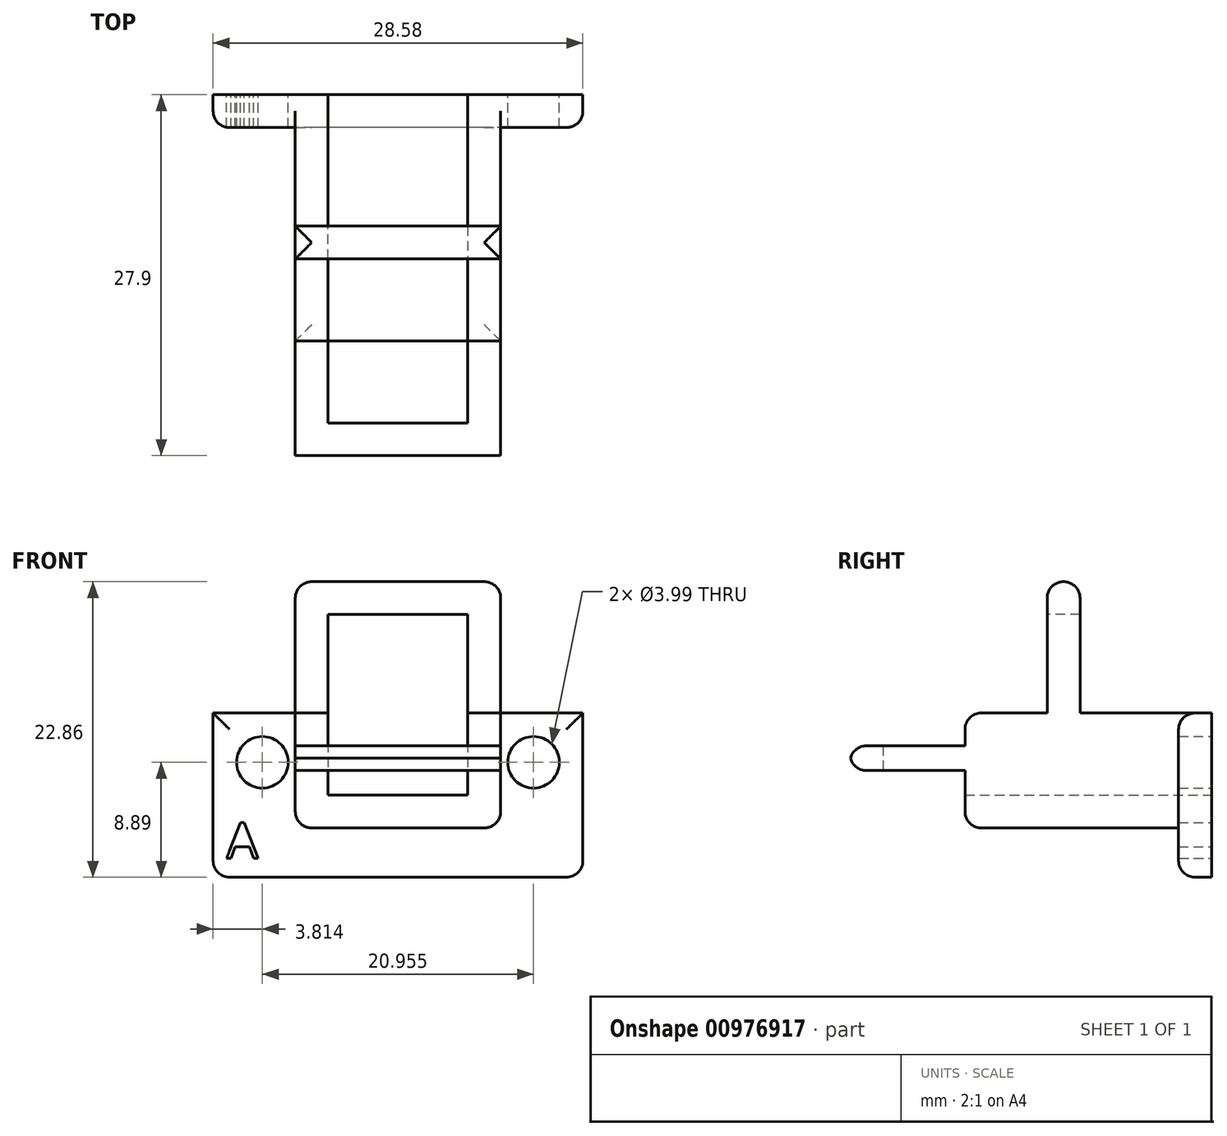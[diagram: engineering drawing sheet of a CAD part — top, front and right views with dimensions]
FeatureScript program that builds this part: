
annotation { "Feature Type Name" : "Feature", "Feature Type Description" : "" }
export const myFeature = defineFeature(function(context is Context, id is Id, definition is map)
    precondition{}
    {
        {
            var Q0;
            Q0=qCreatedBy(makeId("Front.planeOp"),FACE);
            var sketch = newSketch(context, id + "F0", { "sketchPlane" : qUnion([Q0])});
            skLineSegment(sketch, "E0", {"start": v(-23.2, 0) * mm, "end": v(-23.2, -6.35) * mm});
            skLineSegment(sketch, "E1", {"start": v(-12.41, 0) * mm, "end": v(-12.41, -6.35) * mm});
            skLineSegment(sketch, "E2", {"start": v(-23.2, -6.35) * mm, "end": v(-12.41, -6.35) * mm});
            skLineSegment(sketch, "E3", {"start": v(-12.41, 0) * mm, "end": v(-9.87, 0) * mm});
            skLineSegment(sketch, "E4", {"start": v(-9.87, 0) * mm, "end": v(-9.87, -8.89) * mm});
            skLineSegment(sketch, "E5", {"start": v(-9.87, -8.89) * mm, "end": v(-25.75, -8.89) * mm});
            skLineSegment(sketch, "E6", {"start": v(-25.75, -8.89) * mm, "end": v(-25.75, 0) * mm});
            skLineSegment(sketch, "E7", {"start": v(-25.75, 0) * mm, "end": v(-23.2, 0) * mm});
            skLineSegment(sketch, "E8", {"start": v(-9.87, 0) * mm, "end": v(-3.52, 0) * mm});
            skLineSegment(sketch, "E9", {"start": v(-3.52, 0) * mm, "end": v(-3.52, -12.7) * mm});
            skLineSegment(sketch, "E10", {"start": v(-3.52, -12.7) * mm, "end": v(-32.1, -12.7) * mm});
            skLineSegment(sketch, "E11", {"start": v(-32.1, -12.7) * mm, "end": v(-32.1, 0) * mm});
            skLineSegment(sketch, "E12", {"start": v(-32.1, 0) * mm, "end": v(-25.75, 0) * mm});
            skCircle(sketch, "E13", {"center": v(-28.29, -3.81) * mm, "radius": 2 * mm});
            skCircle(sketch, "E14", {"center": v(-7.33, -3.81) * mm, "radius": 2 * mm});
            skText(sketch, "E15", { "text": "A", "fontName": "OpenSans-Regular.ttf"});
            const initialGuessF0  = {"E15": [-0.03105, -0.01123, 1, 0, 0.00276]};
            skSetInitialGuess(sketch, initialGuessF0);
            skSolve(sketch);
        }
        {
            var Q0;
            Q0=makeQuery(id+"F0.imprint","IMPRINT",FACE,{"disambiguationData":[TD([[makeQuery(id+"F0.imprint","IMPRINT",EDGE,{"derivedFrom":sQuery(id+"F0.wireOp",EDGE,"E0")}),-1.0]])]});
            extrude(context, id + "F1", {"entities" : qUnion([Q0]), "depth" : 19.05 * mm, "offsetDistance" : 25.4 * mm});
        }
        {
            var Q0;
            Q0=makeQuery(id+"F0.imprint","IMPRINT",FACE,{"disambiguationData":[TD([[makeQuery(id+"F0.imprint","IMPRINT",EDGE,{"derivedFrom":sQuery(id+"F0.wireOp",EDGE,"E4")}),1.0]])]});
            extrude(context, id + "F2", {"entities" : qUnion([Q0]), "operationType" : NewBodyOperationType.ADD, "depth" : 2.54 * mm, "offsetDistance" : 25.4 * mm});
        }
        {
            var Q0;
            Q0=makeQuery(id+"F1.opExtrude","CAP_FACE",FACE,{"disambiguationData":[OSD([sQuery(id+"F0.wireOp",EDGE,"E0"),sQuery(id+"F0.wireOp",EDGE,"E1"),sQuery(id+"F0.wireOp",EDGE,"E2"),sQuery(id+"F0.wireOp",EDGE,"E3"),sQuery(id+"F0.wireOp",EDGE,"E4"),sQuery(id+"F0.wireOp",EDGE,"E5"),sQuery(id+"F0.wireOp",EDGE,"E6"),sQuery(id+"F0.wireOp",EDGE,"E7")])],"isStart":false});
            var sketch = newSketch(context, id + "F3", { "sketchPlane" : qUnion([Q0])});
            skLineSegment(sketch, "E16", {"start": v(-25.75, -2.54) * mm, "end": v(-9.87, -2.54) * mm});
            skLineSegment(sketch, "E17", {"start": v(-9.87, -2.54) * mm, "end": v(-9.87, -4.45) * mm});
            skLineSegment(sketch, "E18", {"start": v(-9.87, -4.45) * mm, "end": v(-25.75, -4.45) * mm});
            skSolve(sketch);
        }
        {
            var Q0;
            {var subQ0=sQuery(id+"F3.wireOp",EDGE,"E17");Q0=makeQuery(id+"F3.imprint","IMPRINT",FACE,{"disambiguationData":[TD([[makeQuery(id+"F3.imprint","IMPRINT",EDGE,{"derivedFrom":subQ0}),-1.0]])]});}
            var Q1;
            {var subQ0=sQuery(id+"F3.wireOp",EDGE,"E16");var subQ1=makeQuery(id+"F1.opExtrude","CAP_EDGE",EDGE,{"disambiguationData":[OSD([sQuery(id+"F0.wireOp",EDGE,"E6")])],"isStart":false});var subQ2=makeQuery(id+"F3.imprint","INTERSECT",VERTEX,{"derivedFrom":[subQ1,subQ0]});Q1=makeQuery(id+"F3.imprint","IMPRINT",FACE,{"disambiguationData":[TD([[makeQuery(id+"F3.imprint","IMPRINT",EDGE,{"disambiguationData":[TD([[subQ2,-1.0]])],"derivedFrom":subQ0}),-1.0]])]});}
            extrude(context, id + "F4", {"entities" : qUnion([Q0, Q1]), "operationType" : NewBodyOperationType.ADD, "depth" : 8.9 * mm, "offsetDistance" : 25.4 * mm});
        }
        {
            var Q0;
            {var subQ0=sQuery(id+"F0.wireOp",EDGE,"E1");Q0=makeQuery(id+"F4.boolean.opBoolean","MERGE",FACE,{"derivedFrom":[makeQuery(id+"F1.opExtrude","SWEPT_FACE",FACE,{"disambiguationData":[OSD([subQ0])]}),makeQuery(id+"F4.opExtrude","SWEPT_FACE",FACE,{"disambiguationData":[OSD([subQ0])]})]});}
            var sketch = newSketch(context, id + "F5", { "sketchPlane" : qUnion([Q0])});
            skLineSegment(sketch, "E19", {"start": v(25.4, -2.54) * mm, "end": v(25.4, -4.44) * mm});
            skSolve(sketch);
        }
        {
            var Q0;
            {var subQ0=sQuery(id+"F5.wireOp",EDGE,"E19");Q0=makeQuery(id+"F5.imprint","IMPRINT",FACE,{"disambiguationData":[TD([[makeQuery(id+"F5.imprint","IMPRINT",EDGE,{"derivedFrom":subQ0}),1.0]])]});}
            extrude(context, id + "F6", {"entities" : qUnion([Q0]), "operationType" : NewBodyOperationType.ADD, "depth" : 11.43 * mm, "offsetDistance" : 25.4 * mm});
        }
        {
            var Q0;
            Q0=makeQuery(id+"F2.boolean.opBoolean","MERGE",FACE,{"derivedFrom":[makeQuery(id+"F1.opExtrude","SWEPT_FACE",FACE,{"disambiguationData":[OSD([sQuery(id+"F0.wireOp",EDGE,"E7")])]}),makeQuery(id+"F2.opExtrude","SWEPT_FACE",FACE,{"disambiguationData":[OSD([sQuery(id+"F0.wireOp",EDGE,"E12")])]})]});
            var sketch = newSketch(context, id + "F7", { "sketchPlane" : qUnion([Q0])});
            skLineSegment(sketch, "E20", {"start": v(-25.75, -10.16) * mm, "end": v(-23.2, -10.16) * mm});
            skLineSegment(sketch, "E21", {"start": v(-25.75, -12.7) * mm, "end": v(-23.2, -12.7) * mm});
            skSolve(sketch);
        }
        {
            var Q0;
            Q0=makeQuery(id+"F2.boolean.opBoolean","MERGE",FACE,{"derivedFrom":[makeQuery(id+"F1.opExtrude","SWEPT_FACE",FACE,{"disambiguationData":[OSD([sQuery(id+"F0.wireOp",EDGE,"E3")])]}),makeQuery(id+"F2.opExtrude","SWEPT_FACE",FACE,{"disambiguationData":[OSD([sQuery(id+"F0.wireOp",EDGE,"E8")])]})]});
            var sketch = newSketch(context, id + "F8", { "sketchPlane" : qUnion([Q0])});
            skLineSegment(sketch, "E22", {"start": v(-12.41, -12.7) * mm, "end": v(-9.87, -12.7) * mm});
            skLineSegment(sketch, "E23", {"start": v(-12.41, -10.16) * mm, "end": v(-9.87, -10.16) * mm});
            skSolve(sketch);
        }
        {
            var Q0;
            {var subQ0=sQuery(id+"F7.wireOp",EDGE,"E20");Q0=makeQuery(id+"F7.imprint","IMPRINT",FACE,{"disambiguationData":[TD([[makeQuery(id+"F7.imprint","IMPRINT",EDGE,{"derivedFrom":subQ0}),-1.0]])]});}
            var Q1;
            {var subQ0=sQuery(id+"F8.wireOp",EDGE,"E22");Q1=makeQuery(id+"F8.imprint","IMPRINT",FACE,{"disambiguationData":[TD([[makeQuery(id+"F8.imprint","IMPRINT",EDGE,{"derivedFrom":subQ0}),1.0]])]});}
            extrude(context, id + "F9", {"entities" : qUnion([Q0, Q1]), "operationType" : NewBodyOperationType.ADD, "depth" : 10.16 * mm, "offsetDistance" : 25.4 * mm});
        }
        {
            var Q0;
            {var subQ0=sQuery(id+"F0.wireOp",EDGE,"E0");Q0=makeQuery(id+"F9.boolean.opBoolean","MERGE",FACE,{"derivedFrom":[makeQuery(id+"F4.boolean.opBoolean","MERGE",FACE,{"derivedFrom":[makeQuery(id+"F1.opExtrude","SWEPT_FACE",FACE,{"disambiguationData":[OSD([subQ0])]}),makeQuery(id+"F4.opExtrude","SWEPT_FACE",FACE,{"disambiguationData":[OSD([subQ0])]})]}),makeQuery(id+"F9.opExtrude","SWEPT_FACE",FACE,{"disambiguationData":[OSD([subQ0,sQuery(id+"F0.wireOp",EDGE,"E7")])]})]});}
            var sketch = newSketch(context, id + "F10", { "sketchPlane" : qUnion([Q0])});
            skLineSegment(sketch, "E24", {"start": v(-12.7, 7.62) * mm, "end": v(-10.16, 7.62) * mm});
            skSolve(sketch);
        }
        {
            var Q0;
            {var subQ0=sQuery(id+"F10.wireOp",EDGE,"E24");Q0=makeQuery(id+"F10.imprint","IMPRINT",FACE,{"disambiguationData":[TD([[makeQuery(id+"F10.imprint","IMPRINT",EDGE,{"derivedFrom":subQ0}),1.0]])]});}
            extrude(context, id + "F11", {"entities" : qUnion([Q0]), "operationType" : NewBodyOperationType.ADD, "depth" : 11.43 * mm, "offsetDistance" : 25.4 * mm});
        }
        {
            var Q0;
            Q0=makeQuery(id+"F2.opExtrude","CAP_EDGE",EDGE,{"disambiguationData":[OSD([sQuery(id+"F0.wireOp",EDGE,"E12")])],"isStart":false});
            var Q1;
            Q1=makeQuery(id+"F2.opExtrude","CAP_EDGE",EDGE,{"disambiguationData":[OSD([sQuery(id+"F0.wireOp",EDGE,"E11")])],"isStart":false});
            var Q2;
            Q2=makeQuery(id+"F2.opExtrude","CAP_EDGE",EDGE,{"disambiguationData":[OSD([sQuery(id+"F0.wireOp",EDGE,"E10")])],"isStart":false});
            var Q3;
            Q3=makeQuery(id+"F2.opExtrude","CAP_EDGE",EDGE,{"disambiguationData":[OSD([sQuery(id+"F0.wireOp",EDGE,"E8")])],"isStart":false});
            var Q4;
            Q4=makeQuery(id+"F2.opExtrude","SWEPT_EDGE",EDGE,{"disambiguationData":[OSD([sQuery(id+"F0.wireOp",EDGE,"E9"),sQuery(id+"F0.wireOp",EDGE,"E10")])]});
            var Q5;
            Q5=makeQuery(id+"F2.opExtrude","SWEPT_EDGE",EDGE,{"disambiguationData":[OSD([sQuery(id+"F0.wireOp",EDGE,"E10"),sQuery(id+"F0.wireOp",EDGE,"E11")])]});
            var Q6;
            Q6=makeQuery(id+"F2.opExtrude","CAP_EDGE",EDGE,{"disambiguationData":[OSD([sQuery(id+"F0.wireOp",EDGE,"E9")])],"isStart":false});
            var Q7;
            Q7=makeQuery(id+"F1.opExtrude","SWEPT_EDGE",EDGE,{"disambiguationData":[OSD([sQuery(id+"F0.wireOp",EDGE,"E4"),sQuery(id+"F0.wireOp",EDGE,"E5")])]});
            var Q8;
            Q8=makeQuery(id+"F1.opExtrude","SWEPT_EDGE",EDGE,{"disambiguationData":[OSD([sQuery(id+"F0.wireOp",EDGE,"E5"),sQuery(id+"F0.wireOp",EDGE,"E6")])]});
            var Q9;
            {var subQ0=sQuery(id+"F3.wireOp",EDGE,"E16");var subQ1=sQuery(id+"F0.wireOp",EDGE,"E1");Q9=makeQuery(id+"F6.boolean.opBoolean","MERGE",EDGE,{"derivedFrom":[makeQuery(id+"F4.opExtrude","CAP_EDGE",EDGE,{"disambiguationData":[OSD([subQ0]),TDD([makeQuery(id+"F3.imprint","IMPRINT",EDGE,{"disambiguationData":[TD([[makeQuery(id+"F3.imprint","INTERSECT",VERTEX,{"derivedFrom":[makeQuery(id+"F1.opExtrude","CAP_EDGE",EDGE,{"disambiguationData":[OSD([sQuery(id+"F0.wireOp",EDGE,"E6")])],"isStart":false}),subQ0]}),-1.0]])],"derivedFrom":subQ0})])],"isStart":false}),makeQuery(id+"F4.opExtrude","CAP_EDGE",EDGE,{"disambiguationData":[OSD([subQ0]),TDD([makeQuery(id+"F3.imprint","IMPRINT",EDGE,{"disambiguationData":[TD([[makeQuery(id+"F3.imprint","INTERSECT",VERTEX,{"derivedFrom":[makeQuery(id+"F1.opExtrude","CAP_EDGE",EDGE,{"disambiguationData":[OSD([subQ1])],"isStart":false}),subQ0]}),-1.0]])],"derivedFrom":subQ0})])],"isStart":false}),makeQuery(id+"F6.opExtrude","SWEPT_EDGE",EDGE,{"disambiguationData":[OSD([subQ1,subQ0])]})]});}
            var Q10;
            Q10=makeQuery(id+"F1.opExtrude","CAP_EDGE",EDGE,{"disambiguationData":[OSD([sQuery(id+"F0.wireOp",EDGE,"E5")])],"isStart":false});
            var Q11;
            {var subQ0=sQuery(id+"F3.wireOp",EDGE,"E18");var subQ1=sQuery(id+"F0.wireOp",EDGE,"E1");Q11=makeQuery(id+"F6.boolean.opBoolean","MERGE",EDGE,{"derivedFrom":[makeQuery(id+"F4.opExtrude","CAP_EDGE",EDGE,{"disambiguationData":[OSD([subQ0]),TDD([makeQuery(id+"F3.imprint","IMPRINT",EDGE,{"disambiguationData":[TD([[makeQuery(id+"F3.imprint","INTERSECT",VERTEX,{"derivedFrom":[makeQuery(id+"F1.opExtrude","CAP_EDGE",EDGE,{"disambiguationData":[OSD([subQ1])],"isStart":false}),subQ0]}),1.0]])],"derivedFrom":subQ0})])],"isStart":false}),makeQuery(id+"F4.opExtrude","CAP_EDGE",EDGE,{"disambiguationData":[OSD([subQ0]),TDD([makeQuery(id+"F3.imprint","IMPRINT",EDGE,{"disambiguationData":[TD([[makeQuery(id+"F3.imprint","INTERSECT",VERTEX,{"derivedFrom":[makeQuery(id+"F1.opExtrude","CAP_EDGE",EDGE,{"disambiguationData":[OSD([sQuery(id+"F0.wireOp",EDGE,"E6")])],"isStart":false}),subQ0]}),1.0]])],"derivedFrom":subQ0})])],"isStart":false}),makeQuery(id+"F6.opExtrude","SWEPT_EDGE",EDGE,{"disambiguationData":[OSD([subQ1,subQ0])]})]});}
            var Q12;
            {var subQ0=sQuery(id+"F7.wireOp",EDGE,"E21");Q12=makeQuery(id+"F11.boolean.opBoolean","MERGE",EDGE,{"derivedFrom":[makeQuery(id+"F9.opExtrude","CAP_EDGE",EDGE,{"disambiguationData":[OSD([subQ0])],"isStart":false}),makeQuery(id+"F9.opExtrude","CAP_EDGE",EDGE,{"disambiguationData":[OSD([sQuery(id+"F8.wireOp",EDGE,"E22")])],"isStart":false}),makeQuery(id+"F11.opExtrude","SWEPT_EDGE",EDGE,{"disambiguationData":[OSD([sQuery(id+"F0.wireOp",EDGE,"E0"),sQuery(id+"F0.wireOp",EDGE,"E7"),subQ0])]})]});}
            var Q13;
            {var subQ0=sQuery(id+"F7.wireOp",EDGE,"E20");Q13=makeQuery(id+"F11.boolean.opBoolean","MERGE",EDGE,{"derivedFrom":[makeQuery(id+"F9.opExtrude","CAP_EDGE",EDGE,{"disambiguationData":[OSD([subQ0])],"isStart":false}),makeQuery(id+"F9.opExtrude","CAP_EDGE",EDGE,{"disambiguationData":[OSD([sQuery(id+"F8.wireOp",EDGE,"E23")])],"isStart":false}),makeQuery(id+"F11.opExtrude","SWEPT_EDGE",EDGE,{"disambiguationData":[OSD([sQuery(id+"F0.wireOp",EDGE,"E0"),sQuery(id+"F0.wireOp",EDGE,"E7"),subQ0])]})]});}
            var Q14;
            Q14=makeQuery(id+"F1.opExtrude","CAP_EDGE",EDGE,{"disambiguationData":[OSD([sQuery(id+"F0.wireOp",EDGE,"E7")])],"isStart":false});
            var Q15;
            Q15=makeQuery(id+"F1.opExtrude","CAP_EDGE",EDGE,{"disambiguationData":[OSD([sQuery(id+"F0.wireOp",EDGE,"E3")])],"isStart":false});
            var Q16;
            Q16=makeQuery(id+"F9.opExtrude","CAP_EDGE",EDGE,{"disambiguationData":[OSD([sQuery(id+"F0.wireOp",EDGE,"E6"),sQuery(id+"F0.wireOp",EDGE,"E7"),sQuery(id+"F0.wireOp",EDGE,"E12")])],"isStart":false});
            var Q17;
            Q17=makeQuery(id+"F9.opExtrude","CAP_EDGE",EDGE,{"disambiguationData":[OSD([sQuery(id+"F0.wireOp",EDGE,"E3"),sQuery(id+"F0.wireOp",EDGE,"E4"),sQuery(id+"F0.wireOp",EDGE,"E8")])],"isStart":false});
            fillet(context, id + "F12", {"entities" : qUnion([Q0, Q1, Q2, Q3, Q4, Q5, Q6, Q7, Q8, Q9, Q10, Q11, Q12, Q13, Q14, Q15, Q16, Q17]), "radius" : 1.27 * mm, "tangentPropagation" : true, "allowEdgeOverflow" : false});
        }
    });
